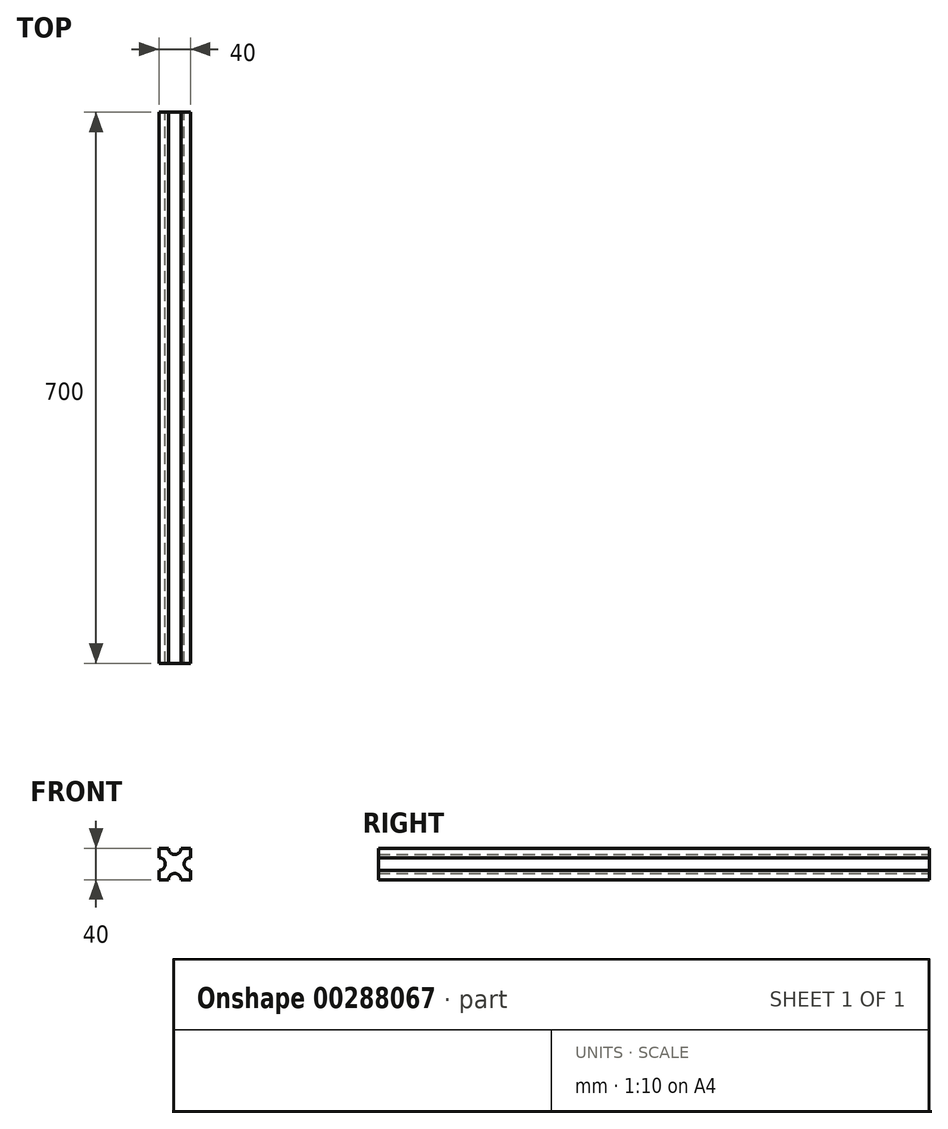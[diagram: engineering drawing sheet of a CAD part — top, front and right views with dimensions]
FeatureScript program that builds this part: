
annotation { "Feature Type Name" : "Feature", "Feature Type Description" : "" }
export const myFeature = defineFeature(function(context is Context, id is Id, definition is map)
    precondition{}
    {
        {
            var Q0;
            Q0=qCreatedBy(makeId("Front.planeOp"),FACE);
            var sketch = newSketch(context, id + "F0", { "sketchPlane" : qUnion([Q0])});
            skLineSegment(sketch, "E0.bottom", {"start": v(20, -20) * mm, "end": v(-20, -20) * mm});
            skLineSegment(sketch, "E0.top", {"start": v(20, 20) * mm, "end": v(-20, 20) * mm});
            skLineSegment(sketch, "E0.left", {"start": v(20, -20) * mm, "end": v(20, 20) * mm});
            skLineSegment(sketch, "E0.right", {"start": v(-20, -20) * mm, "end": v(-20, 20) * mm});
            skPoint(sketch, "E0.middle", {"position": v(0, 0) * mm});
            skCircle(sketch, "E1", {"center": v(0, 20) * mm, "radius": 8 * mm});
            skCircle(sketch, "E2", {"center": v(-20, 0) * mm, "radius": 8 * mm});
            skCircle(sketch, "E3", {"center": v(0, -20) * mm, "radius": 8 * mm});
            skCircle(sketch, "E4", {"center": v(20, 0) * mm, "radius": 8 * mm});
            skSolve(sketch);
        }
        {
            var Q0;
            {var subQ4=sQuery(id+"F0.wireOp",EDGE,"E0.bottom");var subQ6=sQuery(id+"F0.wireOp",EDGE,"E0.left");var subQ11=makeQuery(id+"F0.imprint","INTERSECT",VERTEX,{"derivedFrom":[subQ4,subQ6]});Q0=makeQuery(id+"F0.imprint","IMPRINT",FACE,{"disambiguationData":[TD([[makeQuery(id+"F0.imprint","IMPRINT",EDGE,{"disambiguationData":[TD([[subQ11,-1.0]])],"derivedFrom":subQ4}),-1.0]])]});}
            extrude(context, id + "F1", {"entities" : qUnion([Q0]), "depth" : 700 * mm});
        }
    });
